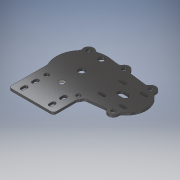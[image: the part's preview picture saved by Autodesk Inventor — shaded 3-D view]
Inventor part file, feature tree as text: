
AUTODESK INVENTOR PART (.ipt)
format: ipt  version: 2017 (Build 210142000, 142)  size: 358,400 bytes
history: native  units: mm
features: extrude x8, sketch x6, fillet x2, other x1, mirror x1
ambient origin geometry x8: Origin, YZ Plane, XZ Plane, XY Plane, X Axis, Y Axis, Z Axis, Center Point
bodies: Body1 (feature_tree)
feature tree (18):
  other  "Sólido1"
  extrude  "Extrusión1"  Depth=88.9mm
  sketch  "Boceto2"  dims[d2=203.2mm d3=22.225mm d4=22.225mm]
  extrude  "Extrusión2"  Depth=22.225mm
  fillet  "Empalme1"  Radius=22.225mm
  sketch  "Boceto3"  dims[d7=22.225mm d8=22.225mm]
  extrude  "Extrusión3"  Depth=22.225mm
  extrude  "Extrusión4"  TaperAngle=0.0deg  [1 undecoded]
  extrude  "Extrusión5"  Depth=5.0mm TaperAngle=0.0deg
  extrude  "Extrusión6"  Depth=6.35mm
  extrude  "Extrusión7"  Depth=6.35mm
  mirror  "Simetría1"
  fillet  "Empalme2"  Radius=9.525mm
  extrude  "Extrusión8"  Depth=6.35mm
  sketch  "Boceto1"  dims[d0=114.3mm d1=88.9mm]
  sketch  "Boceto4"  dims[d11=22.225mm d13=0.0mm]
  sketch  "Boceto5"  dims[d14=22.225mm d16=5.0mm d17=0.0mm]
  sketch  "Boceto7"  dims[d18=9.525mm d19=9.525mm d20=9.525mm d21=9.525mm d22=9.525mm d23=9.525mm d24=25.4mm d25=0.0mm d26=6.35mm d27=12.7mm d28=12.7mm d29=44.45mm d30=44.45mm d31=31.75mm d32=31.75mm d33=14.2875mm d34=12.7mm d35=12.7mm d36=45.0mm d37=45.0mm d38=25.4mm d39=0.0mm d40=12.7mm d41=56.0mm d42=56.0mm d43=28.0mm d44=28.0mm d45=0.0mm d46=93.4212mm d47=47.5mm d48=47.5mm d49=23.75mm d50=23.75mm d57=5.55625mm d58=5.159375mm d59=5.55625mm d60=5.55625mm d61=5.159375mm d62=5.159375mm d63=5.55625mm d64=5.159375mm d65=0.0mm d66=5.55625mm d67=5.55625mm d68=5.159375mm d69=5.159375mm d70=0.0mm d71=5.55625mm d72=5.55625mm d73=5.159375mm d74=5.159375mm d75=0.0mm d76=25.4mm d77=0.0mm d78=12.7mm d79=12.7mm d80=5.159375mm d81=5.159375mm d82=101.6mm d84=171.45mm d85=95.25mm d86=25.4mm d87=0.0mm d88=25.4mm d89=0.0mm d90=8.73125mm d91=8.73125mm d92=19.05mm d93=44.45mm d94=38.1mm d95=0.0mm d96=8.73125mm d97=8.73125mm d98=19.05mm d99=19.05mm d100=12.7mm d101=0.0mm d102=25.4mm d103=0.0mm d104=6.35mm d105=25.4mm d106=0.0mm]
note: 1 required parameter value undecoded (feature->parameter linkage not recoverable at this tier; creation-order binding heuristic only, values carry confidence <= 0.55)
